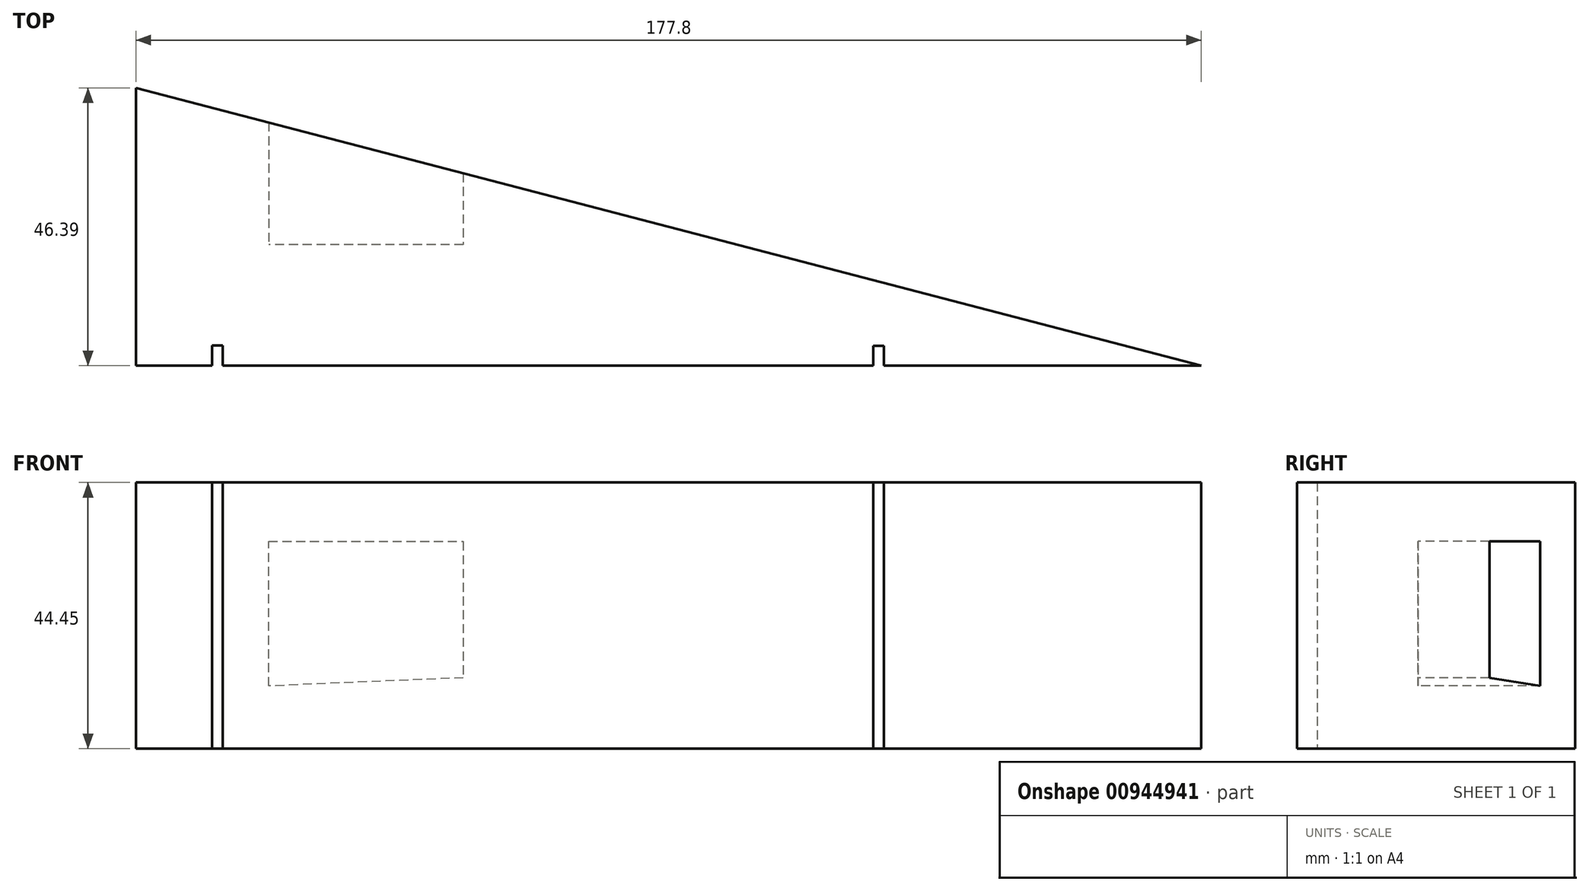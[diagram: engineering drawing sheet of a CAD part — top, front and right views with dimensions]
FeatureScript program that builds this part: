
annotation { "Feature Type Name" : "Feature", "Feature Type Description" : "" }
export const myFeature = defineFeature(function(context is Context, id is Id, definition is map)
    precondition{}
    {
        {
            var Q0;
            Q0=qCreatedBy(makeId("Top.planeOp"),FACE);
            var sketch = newSketch(context, id + "F0", { "sketchPlane" : qUnion([Q0])});
            skLineSegment(sketch, "E0", {"start": v(-42.16, 26.2) * mm, "end": v(-42.16, -20.2) * mm});
            skLineSegment(sketch, "E1", {"start": v(-42.16, -20.2) * mm, "end": v(135.64, -20.2) * mm});
            skLineSegment(sketch, "E2", {"start": v(-42.16, 26.2) * mm, "end": v(135.64, -20.2) * mm});
            skSolve(sketch);
        }
        {
            var Q0;
            Q0=makeQuery(id+"F0.imprint","IMPRINT",FACE,{"disambiguationData":[TD([[makeQuery(id+"F0.imprint","IMPRINT",EDGE,{"derivedFrom":sQuery(id+"F0.wireOp",EDGE,"E0")}),1.0]])]});
            extrude(context, id + "F1", {"entities" : qUnion([Q0]), "depth" : 44.45 * mm, "offsetDistance" : 25.4 * mm});
        }
        {
            var Q0;
            Q0=qCreatedBy(makeId("Front.planeOp"),FACE);
            var sketch = newSketch(context, id + "F2", { "sketchPlane" : qUnion([Q0])});
            skLineSegment(sketch, "E3", {"start": v(-20.01, 10.48) * mm, "end": v(-20.01, 34.61) * mm});
            skLineSegment(sketch, "E4", {"start": v(-20.01, 34.61) * mm, "end": v(12.47, 34.61) * mm});
            skLineSegment(sketch, "E5", {"start": v(12.47, 34.61) * mm, "end": v(12.47, 11.85) * mm});
            skLineSegment(sketch, "E6", {"start": v(12.47, 11.85) * mm, "end": v(-20.01, 10.48) * mm});
            skSolve(sketch);
        }
        {
            var Q0;
            Q0 = qSketchRegion(id + "F2", true);
            var Q1;
            Q1=makeQuery(id+"F1.opExtrude","SWEPT_FACE",FACE,{"disambiguationData":[OSD([sQuery(id+"F0.wireOp",EDGE,"E2")])]});
            extrude(context, id + "F3", {"entities" : qUnion([Q0, Q1]), "operationType" : NewBodyOperationType.REMOVE, "oppositeDirection" : true, "depth" : 25.4 * mm, "offsetDistance" : 25.4 * mm});
        }
        {
            var Q0;
            Q0=qCreatedBy(makeId("Top.planeOp"),FACE);
            var sketch = newSketch(context, id + "F4", { "sketchPlane" : qUnion([Q0])});
            skLineSegment(sketch, "E7", {"start": v(-29.46, -20.2) * mm, "end": v(-29.46, -16.84) * mm});
            skLineSegment(sketch, "E8", {"start": v(-29.46, -16.84) * mm, "end": v(-27.71, -16.84) * mm});
            skLineSegment(sketch, "E9", {"start": v(-27.71, -16.84) * mm, "end": v(-27.71, -20.2) * mm});
            skLineSegment(sketch, "E10", {"start": v(-27.71, -20.2) * mm, "end": v(-29.46, -20.2) * mm});
            skSolve(sketch);
        }
        {
            var Q0;
            Q0 = qSketchRegion(id + "F4", true);
            extrude(context, id + "F5", {"entities" : qUnion([Q0]), "operationType" : NewBodyOperationType.REMOVE, "endBound" : BoundingType.SYMMETRIC, "depth" : 124.51 * mm, "offsetDistance" : 25.4 * mm});
        }
        {
            var Q0;
            Q0=qCreatedBy(makeId("Top.planeOp"),FACE);
            var sketch = newSketch(context, id + "F6", { "sketchPlane" : qUnion([Q0])});
            skLineSegment(sketch, "E11", {"start": v(80.92, -20.2) * mm, "end": v(80.92, -16.84) * mm});
            skLineSegment(sketch, "E12", {"start": v(80.92, -16.84) * mm, "end": v(82.68, -16.84) * mm});
            skLineSegment(sketch, "E13", {"start": v(82.68, -16.84) * mm, "end": v(82.68, -20.2) * mm});
            skLineSegment(sketch, "E14", {"start": v(80.92, -20.2) * mm, "end": v(82.68, -20.2) * mm});
            skSolve(sketch);
        }
        {
            var Q0;
            Q0=makeQuery(id+"F6.imprint","IMPRINT",FACE,{"disambiguationData":[TD([[makeQuery(id+"F6.imprint","IMPRINT",EDGE,{"derivedFrom":sQuery(id+"F6.wireOp",EDGE,"E11")}),-1.0]])]});
            extrude(context, id + "F7", {"entities" : qUnion([Q0]), "operationType" : NewBodyOperationType.REMOVE, "endBound" : BoundingType.SYMMETRIC, "depth" : 138.18 * mm, "offsetDistance" : 25.4 * mm});
        }
    });
